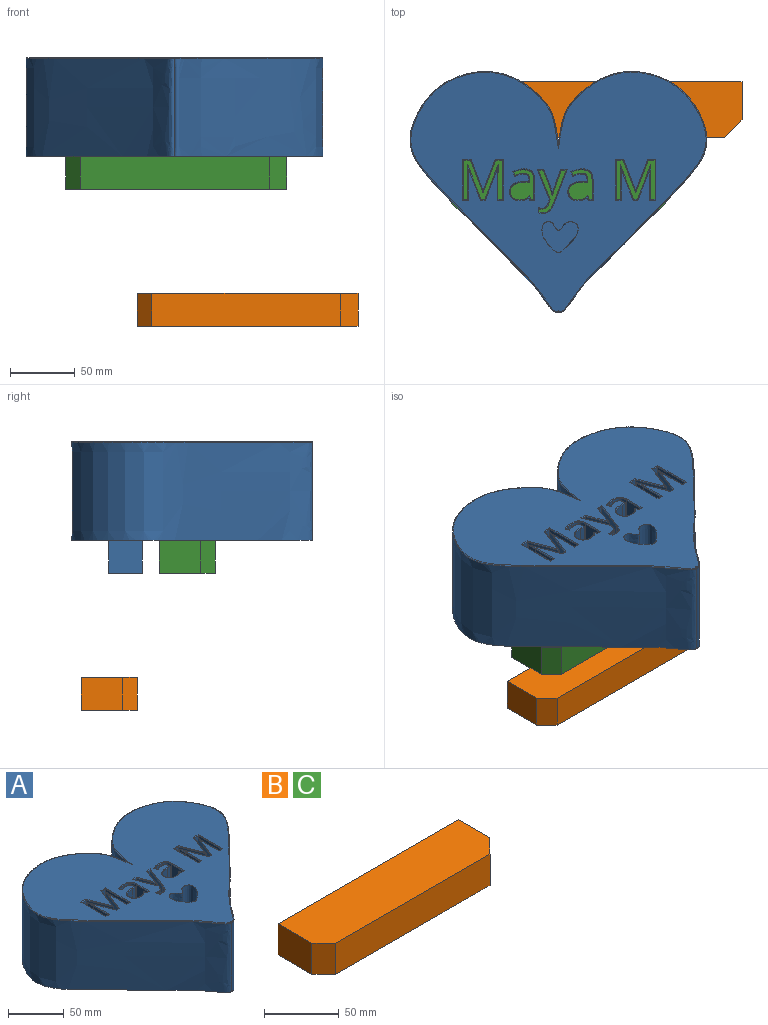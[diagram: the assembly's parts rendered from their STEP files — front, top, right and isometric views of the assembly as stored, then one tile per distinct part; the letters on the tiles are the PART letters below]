
ASSEMBLY  parts=3 mates=2
PART A: 183 faces, bbox 231.7x188.4x101.6 mm
  f0: plane 231.66x188.38mm, normal (0,0,-1), area 24079.3mm2, adj f2,f3,f4,f5,f6,f7,f8,f9
  f1: plane 227.62x184.41mm, normal (0,0,1), area 23045.1mm2, adj f94,f95,f96,f97,f98,f99,f100,f101
  f2: extruded ~184.82x114.31mm, area 26534mm2, adj f0,f3,f176
  f3: extruded ~184.82x114.31mm, area 26534mm2, adj f0,f2,f175
  f4: plane 75.57x3.68mm, normal (0,-1,0), area 278.4mm2, adj f0,f5,f19,f174
  f5: plane 75.57x22.78mm, normal (0.93,0.37,0), area 1854.8mm2, adj f0,f4,f6,f173
  f6: plane 75.57x3.22mm, normal (0.93,-0.37,0), area 261.5mm2, adj f0,f5,f7,f171
  f7: extruded ~75.57x5.05mm, area 520.7mm2, adj f0,f6,f8,f169
  f8: extruded ~75.57x2.54mm, area 193.2mm2, adj f0,f7,f9,f167
  f9: plane 75.57x2.75mm, normal (1,0,0), area 207.4mm2, adj f0,f8,f10,f165
  f10: extruded ~75.57x3.1mm, area 236.5mm2, adj f0,f9,f11,f163
  f11: extruded ~75.57x4.74mm, area 386.3mm2, adj f0,f10,f12,f161
  f12: extruded ~75.57x5.43mm, area 488.2mm2, adj f0,f11,f13,f160
  f13: plane 75.57x25.8mm, normal (-0.94,0.35,0), area 2083.6mm2, adj f0,f12,f14,f162
  f14: plane 75.57x3.68mm, normal (0,-1,0), area 277.9mm2, adj f0,f13,f15,f164
  f15: extruded ~75.57x15.7mm, area 1259.7mm2, adj f0,f14,f16,f166
  f16: extruded ~75.57x3.61mm, area 285.9mm2, adj f0,f15,f17,f168
  f17: plane 75.89x0.18mm, normal (0,-1,0), area 12.5mm2, adj f0,f16,f18,f168,f170
  f18: extruded ~75.57x6.39mm, area 506.9mm2, adj f0,f17,f19,f170
  f19: plane 75.57x12.92mm, normal (-0.93,-0.36,0), area 1045.7mm2, adj f0,f4,f18,f172
  f20: plane 75.57x26.79mm, normal (0.93,0.36,0), area 2167.5mm2, adj f0,f21,f37,f159
  f21: plane 75.57x2.83mm, normal (0,1,0), area 213.9mm2, adj f0,f20,f22,f158
  f22: plane 75.57x26.75mm, normal (-0.93,0.36,0), area 2167mm2, adj f0,f21,f23,f156
  f23: plane 75.89x0.18mm, normal (0,1,0), area 12.5mm2, adj f0,f22,f24,f154,f156
  f24: extruded ~75.57x7.28mm, area 550.4mm2, adj f0,f23,f25,f154
  f25: plane 75.57x19.47mm, normal (1,0,0), area 1471.5mm2, adj f0,f24,f26,f152
  f26: plane 75.57x3.51mm, normal (0,1,0), area 265.4mm2, adj f0,f25,f27,f150
  f27: plane 75.57x30.22mm, normal (-1,0,0), area 2283.7mm2, adj f0,f26,f28,f148
  f28: plane 75.57x5.25mm, normal (0,-1,0), area 396.9mm2, adj f0,f27,f29,f146
  f29: plane 75.57x24.93mm, normal (0.93,-0.36,0), area 2020.1mm2, adj f0,f28,f30,f145
  f30: plane 75.88x0.18mm, normal (0,-1,0), area 12.5mm2, adj f0,f29,f31,f145,f147
  f31: plane 75.57x24.93mm, normal (-0.93,-0.36,0), area 2017.9mm2, adj f0,f30,f32,f147
  f32: plane 75.57x5.29mm, normal (0,-1,0), area 399.9mm2, adj f0,f31,f33,f149
  f33: plane 75.57x30.22mm, normal (1,0,0), area 2283.7mm2, adj f0,f32,f34,f151
  f34: plane 75.57x3.25mm, normal (0,1,0), area 245.4mm2, adj f0,f33,f35,f153
  f35: plane 75.57x19.22mm, normal (-1,0,0), area 1452.5mm2, adj f0,f34,f36,f155
  f36: extruded ~75.57x7.57mm, area 572.4mm2, adj f0,f35,f37,f157
  f37: plane 75.89x0.18mm, normal (0,1,0), area 12.5mm2, adj f0,f20,f36,f157,f159
  f38: plane 75.57x3.23mm, normal (0.98,0.21,0), area 249.3mm2, adj f0,f39,f56,f144
  f39: plane 75.57x2.55mm, normal (0,1,0), area 192.4mm2, adj f0,f38,f40,f143
  f40: plane 75.57x15.47mm, normal (-1,0,0), area 1168.6mm2, adj f0,f39,f41,f141
  f41: extruded ~75.57x5.76mm, area 473.5mm2, adj f0,f40,f42,f139
  f42: extruded ~75.57x6mm, area 484.4mm2, adj f0,f41,f43,f137
  f43: extruded ~75.57x4.01mm, area 306mm2, adj f0,f42,f44,f135
  f44: extruded ~75.57x3.67mm, area 298mm2, adj f0,f43,f45,f133
  f45: plane 75.57x2.63mm, normal (0.93,0.37,0), area 213.9mm2, adj f0,f44,f46,f131
  f46: extruded ~75.57x6.4mm, area 505.4mm2, adj f0,f45,f47,f129
  f47: extruded ~75.57x3.67mm, area 302.4mm2, adj f0,f46,f48,f127
  f48: extruded ~75.57x3.94mm, area 316.6mm2, adj f0,f47,f49,f128
  f49: plane 75.57x1.41mm, normal (1,0,0), area 106.5mm2, adj f0,f48,f50,f130
  f50: plane 75.57x3.84mm, normal (0.03,-1,0), area 290.6mm2, adj f0,f49,f51,f132
  f51: extruded ~75.57x10.97mm, area 1113.9mm2, adj f0,f50,f52,f134
  f52: extruded ~75.57x4.94mm, area 412.8mm2, adj f0,f51,f53,f136
  f53: extruded ~75.57x5.28mm, area 429.9mm2, adj f0,f52,f54,f138
  f54: extruded ~75.57x4.21mm, area 325.6mm2, adj f0,f53,f55,f140
  f55: extruded ~75.57x3.38mm, area 338.8mm2, adj f0,f54,f56,f142
  f56: plane 75.89x0.2mm, normal (0,1,0), area 12.5mm2, adj f0,f38,f55,f142,f144
  f57: plane 75.57x3.23mm, normal (0.98,0.21,0), area 249.3mm2, adj f0,f58,f75,f126
  f58: plane 75.57x2.55mm, normal (0,1,0), area 192.4mm2, adj f0,f57,f59,f125
  f59: plane 75.57x15.47mm, normal (-1,0,0), area 1168.6mm2, adj f0,f58,f60,f123
  f60: extruded ~75.57x5.76mm, area 473.5mm2, adj f0,f59,f61,f121
  f61: extruded ~75.57x6mm, area 484.4mm2, adj f0,f60,f62,f119
  f62: extruded ~75.57x4.01mm, area 306mm2, adj f0,f61,f63,f117
  f63: extruded ~75.57x3.67mm, area 298mm2, adj f0,f62,f64,f115
  f64: plane 75.57x2.63mm, normal (0.93,0.37,0), area 213.9mm2, adj f0,f63,f65,f113
  f65: extruded ~75.57x6.4mm, area 505.4mm2, adj f0,f64,f66,f111
  f66: extruded ~75.57x3.67mm, area 302.4mm2, adj f0,f65,f67,f109
  f67: extruded ~75.57x3.94mm, area 316.6mm2, adj f0,f66,f68,f110
  f68: plane 75.57x1.41mm, normal (1,0,0), area 106.5mm2, adj f0,f67,f69,f112
  f69: plane 75.57x3.84mm, normal (0.03,-1,0), area 290.6mm2, adj f0,f68,f70,f114
  f70: extruded ~75.57x10.97mm, area 1113.9mm2, adj f0,f69,f71,f116
  f71: extruded ~75.57x4.94mm, area 412.8mm2, adj f0,f70,f72,f118
  f72: extruded ~75.57x5.28mm, area 429.9mm2, adj f0,f71,f73,f120
  f73: extruded ~75.57x4.21mm, area 325.6mm2, adj f0,f72,f74,f122
  f74: extruded ~75.57x3.38mm, area 338.8mm2, adj f0,f73,f75,f124
  f75: plane 75.89x0.2mm, normal (0,1,0), area 12.5mm2, adj f0,f57,f74,f124,f126
  f76: plane 75.57x26.79mm, normal (0.93,0.36,0), area 2167.5mm2, adj f0,f77,f93,f108
  f77: plane 75.57x2.83mm, normal (0,1,0), area 213.9mm2, adj f0,f76,f78,f107
  f78: plane 75.57x26.75mm, normal (-0.93,0.36,0), area 2167mm2, adj f0,f77,f79,f105
  f79: plane 75.89x0.18mm, normal (0,1,0), area 12.5mm2, adj f0,f78,f80,f103,f105
  f80: extruded ~75.57x7.28mm, area 550.4mm2, adj f0,f79,f81,f103
  f81: plane 75.57x19.47mm, normal (1,0,0), area 1471.5mm2, adj f0,f80,f82,f101
  f82: plane 75.57x3.51mm, normal (0,1,0), area 265.4mm2, adj f0,f81,f83,f99
  f83: plane 75.57x30.22mm, normal (-1,0,0), area 2283.7mm2, adj f0,f82,f84,f97
  f84: plane 75.57x5.25mm, normal (0,-1,0), area 396.9mm2, adj f0,f83,f85,f95
  f85: plane 75.57x24.93mm, normal (0.93,-0.36,0), area 2020.1mm2, adj f0,f84,f86,f94
  f86: plane 75.88x0.18mm, normal (0,-1,0), area 12.5mm2, adj f0,f85,f87,f94,f96
  f87: plane 75.57x24.93mm, normal (-0.93,-0.36,0), area 2017.9mm2, adj f0,f86,f88,f96
  f88: plane 75.57x5.29mm, normal (0,-1,0), area 399.9mm2, adj f0,f87,f89,f98
  f89: plane 75.57x30.22mm, normal (1,0,0), area 2283.7mm2, adj f0,f88,f90,f100
  f90: plane 75.57x3.25mm, normal (0,1,0), area 245.4mm2, adj f0,f89,f91,f102
  f91: plane 75.57x19.22mm, normal (-1,0,0), area 1452.5mm2, adj f0,f90,f92,f104
  f92: extruded ~75.57x7.57mm, area 572.4mm2, adj f0,f91,f93,f106
  f93: plane 75.89x0.18mm, normal (0,1,0), area 12.5mm2, adj f0,f76,f92,f106,f108
  f94: cylinder r=0.64mm len=25.59mm, axis (0.36,0.93,0), area 26.4mm2, adj f1,f85,f86,f95,f96
  f95: cylinder r=0.64mm len=6.32mm, axis (1,0,0), area 5.8mm2, adj f1,f84,f94,f97
  f96: cylinder r=0.64mm len=25.59mm, axis (0.36,-0.93,0), area 26.4mm2, adj f1,f86,f87,f94,f98
  f97: cylinder r=0.64mm len=31.49mm, axis (0,-1,0), area 30.8mm2, adj f1,f83,f95,f99
  f98: cylinder r=0.64mm len=6.36mm, axis (1,0,0), area 5.8mm2, adj f1,f88,f96,f100
  f99: cylinder r=0.64mm len=4.78mm, axis (-1,0,0), area 4.1mm2, adj f1,f82,f97,f101
  f100: cylinder r=0.64mm len=31.49mm, axis (0,1,0), area 30.8mm2, adj f1,f89,f98,f102
  f101: cylinder r=0.64mm len=20.11mm, axis (0,1,0), area 19.7mm2, adj f1,f81,f99,f103
  f102: cylinder r=0.64mm len=4.52mm, axis (-1,0,0), area 3.9mm2, adj f1,f90,f100,f104
  f103: bspline ~10.89x1.07mm, area 6.1mm2, adj f1,f79,f80,f101,f105
  f104: cylinder r=0.64mm len=19.86mm, axis (0,-1,0), area 19.5mm2, adj f1,f91,f102,f106
  f105: cylinder r=0.64mm len=27.41mm, axis (-0.36,-0.93,0), area 27.6mm2, adj f1,f78,f79,f103,f107
  f106: bspline ~9.93x0.97mm, area 6.4mm2, adj f1,f92,f93,f104,f108
  f107: cylinder r=0.64mm len=3.7mm, axis (-1,0,0), area 3.3mm2, adj f1,f77,f105,f108
  f108: cylinder r=0.64mm len=27.45mm, axis (-0.36,0.93,0), area 27.6mm2, adj f1,f76,f93,f106,f107
  f109: bspline ~5.42x2.18mm, area 3.8mm2, adj f1,f66,f110,f111
  f110: bspline ~6.23x2.17mm, area 4mm2, adj f1,f67,f109,f112
  f111: bspline ~9.07x2.76mm, area 6.9mm2, adj f1,f65,f109,f113
  f112: cylinder r=0.64mm len=1.41mm, axis (0,1,0), area 1.1mm2, adj f1,f68,f110,f114
  f113: cylinder r=0.64mm len=4.02mm, axis (-0.37,0.93,0), area 3.4mm2, adj f1,f64,f111,f115
  f114: cylinder r=0.64mm len=3.86mm, axis (1,0.03,0), area 3.5mm2, adj f1,f69,f112,f116
  f115: bspline ~7.51x3.71mm, area 4.3mm2, adj f1,f63,f113,f117
  f116: bspline ~16.18x10.25mm, area 15.1mm2, adj f1,f70,f114,f118
  f117: bspline ~5.57x1.33mm, area 4.1mm2, adj f1,f62,f115,f119
  f118: bspline ~7.83x3.22mm, area 5.6mm2, adj f1,f71,f116,f120
  f119: bspline ~10x3.31mm, area 6.6mm2, adj f1,f61,f117,f121
  f120: bspline ~7.09x3.13mm, area 5.8mm2, adj f1,f72,f118,f122
  f121: bspline ~9.19x3.4mm, area 6.4mm2, adj f1,f60,f119,f123
  f122: bspline ~6.18x1.76mm, area 4.4mm2, adj f1,f73,f120,f124
  f123: cylinder r=0.64mm len=16.1mm, axis (0,-1,0), area 15.7mm2, adj f1,f59,f121,f125
  f124: bspline ~5.25x4.3mm, area 4.2mm2, adj f1,f74,f75,f122,f126
  f125: cylinder r=0.64mm len=3.7mm, axis (-1,0,0), area 3.1mm2, adj f1,f58,f123,f126
  f126: cylinder r=0.64mm len=3.88mm, axis (-0.21,0.98,0), area 3.2mm2, adj f1,f57,f75,f124,f125
  f127: bspline ~5.42x2.18mm, area 3.8mm2, adj f1,f47,f128,f129
  f128: bspline ~6.23x2.17mm, area 4mm2, adj f1,f48,f127,f130
  f129: bspline ~9.07x2.76mm, area 6.9mm2, adj f1,f46,f127,f131
  f130: cylinder r=0.64mm len=1.41mm, axis (0,1,0), area 1.1mm2, adj f1,f49,f128,f132
  f131: cylinder r=0.64mm len=4.02mm, axis (-0.37,0.93,0), area 3.4mm2, adj f1,f45,f129,f133
  f132: cylinder r=0.64mm len=3.86mm, axis (1,0.03,0), area 3.5mm2, adj f1,f50,f130,f134
  f133: bspline ~7.51x3.71mm, area 4.3mm2, adj f1,f44,f131,f135
  f134: bspline ~16.18x10.25mm, area 15.1mm2, adj f1,f51,f132,f136
  f135: bspline ~5.57x1.33mm, area 4.1mm2, adj f1,f43,f133,f137
  f136: bspline ~7.83x3.22mm, area 5.6mm2, adj f1,f52,f134,f138
  f137: bspline ~10x3.31mm, area 6.6mm2, adj f1,f42,f135,f139
  f138: bspline ~8.76x3.13mm, area 5.8mm2, adj f1,f53,f136,f140
  f139: bspline ~9.19x3.4mm, area 6.4mm2, adj f1,f41,f137,f141
  f140: bspline ~6.18x1.76mm, area 4.4mm2, adj f1,f54,f138,f142
  f141: cylinder r=0.64mm len=16.1mm, axis (0,-1,0), area 15.7mm2, adj f1,f40,f139,f143
  f142: bspline ~5.25x4.3mm, area 4.2mm2, adj f1,f55,f56,f140,f144
  f143: cylinder r=0.64mm len=3.7mm, axis (-1,0,0), area 3.1mm2, adj f1,f39,f141,f144
  f144: cylinder r=0.64mm len=3.88mm, axis (-0.21,0.98,0), area 3.2mm2, adj f1,f38,f56,f142,f143
  f145: cylinder r=0.64mm len=25.59mm, axis (0.36,0.93,0), area 26.4mm2, adj f1,f29,f30,f146,f147
  f146: cylinder r=0.64mm len=6.32mm, axis (1,0,0), area 5.8mm2, adj f1,f28,f145,f148
  f147: cylinder r=0.64mm len=25.59mm, axis (0.36,-0.93,0), area 26.4mm2, adj f1,f30,f31,f145,f149
  f148: cylinder r=0.64mm len=31.49mm, axis (0,-1,0), area 30.8mm2, adj f1,f27,f146,f150
  f149: cylinder r=0.64mm len=6.36mm, axis (1,0,0), area 5.8mm2, adj f1,f32,f147,f151
  f150: cylinder r=0.64mm len=4.78mm, axis (-1,0,0), area 4.1mm2, adj f1,f26,f148,f152
  f151: cylinder r=0.64mm len=31.49mm, axis (0,1,0), area 30.8mm2, adj f1,f33,f149,f153
  f152: cylinder r=0.64mm len=20.11mm, axis (0,1,0), area 19.7mm2, adj f1,f25,f150,f154
  f153: cylinder r=0.64mm len=4.52mm, axis (-1,0,0), area 3.9mm2, adj f1,f34,f151,f155
  f154: bspline ~10.89x1.07mm, area 6.1mm2, adj f1,f23,f24,f152,f156
  f155: cylinder r=0.64mm len=19.86mm, axis (0,-1,0), area 19.5mm2, adj f1,f35,f153,f157
  f156: cylinder r=0.64mm len=27.41mm, axis (-0.36,-0.93,0), area 27.6mm2, adj f1,f22,f23,f154,f158
  f157: bspline ~9.93x0.97mm, area 6.4mm2, adj f1,f36,f37,f155,f159
  f158: cylinder r=0.64mm len=3.7mm, axis (-1,0,0), area 3.3mm2, adj f1,f21,f156,f159
  f159: cylinder r=0.64mm len=27.45mm, axis (-0.36,0.93,0), area 27.6mm2, adj f1,f20,f37,f157,f158
  f160: bspline ~7.16x5.2mm, area 6.6mm2, adj f1,f12,f161,f162
  f161: bspline ~6.96x2.89mm, area 5.3mm2, adj f1,f11,f160,f163
  f162: cylinder r=0.64mm len=26.88mm, axis (-0.35,-0.94,0), area 28mm2, adj f1,f13,f160,f164
  f163: bspline ~6.1x1.5mm, area 3.4mm2, adj f1,f10,f161,f165
  f164: cylinder r=0.64mm len=5.04mm, axis (1,0,0), area 4.3mm2, adj f1,f14,f162,f166
  f165: cylinder r=0.64mm len=4.04mm, axis (0,1,0), area 3.4mm2, adj f1,f9,f163,f167
  f166: bspline ~22.75x8.65mm, area 16.9mm2, adj f1,f15,f164,f168
  f167: bspline ~5.6x1.39mm, area 2.9mm2, adj f1,f8,f165,f169
  f168: bspline ~5.36x2.2mm, area 3.1mm2, adj f1,f16,f17,f166,f170
  f169: bspline ~6.86x4.48mm, area 6.6mm2, adj f1,f7,f167,f171
  f170: bspline ~8.01x3.1mm, area 6.1mm2, adj f1,f17,f18,f168,f172
  f171: cylinder r=0.64mm len=3.46mm, axis (0.37,0.93,0), area 3.3mm2, adj f1,f6,f169,f173
  f172: cylinder r=0.64mm len=13.56mm, axis (0.36,-0.93,0), area 14mm2, adj f1,f19,f170,f174
  f173: cylinder r=0.64mm len=23.89mm, axis (-0.37,0.93,0), area 24.8mm2, adj f1,f5,f171,f174
  f174: cylinder r=0.64mm len=5.06mm, axis (1,0,0), area 4.4mm2, adj f1,f4,f172,f173
  f175: bspline ~185.69x115.29mm, area 351.6mm2, adj f1,f3,f176
  f176: bspline ~185.69x115.29mm, area 351.6mm2, adj f1,f2,f175
  f177: extruded ~50.8x27.95mm, area 4522.2mm2, adj f1,f178
  f178: plane 28.79x24.74mm, normal (0,0,1), area 452.6mm2, adj f177
  f179: plane 25.49x25.4mm, normal (0.86,-0.5,0), area 750mm2, adj f0,f180,f181,f182
  f180: plane 29.53x25.4mm, normal (0.01,1,0), area 750mm2, adj f0,f179,f181,f182
  f181: plane 25.65x25.4mm, normal (-0.87,-0.5,0), area 750mm2, adj f0,f179,f180,f182
  f182: plane 29.53x25.65mm, normal (0,0,-1), area 377.5mm2, adj f179,f180,f181
PART B: 8 faces, bbox 170.2x43.2x25.4 mm
  f0: plane 25.4x11.26mm, normal (-0.71,-0.7,0), area 402.7mm2, adj f1,f5,f6,f7
  f1: plane 145.54x25.4mm, normal (0,-1,0), area 3696.8mm2, adj f0,f2,f6,f7
  f2: plane 25.4x13.67mm, normal (0.71,-0.7,0), area 487.6mm2, adj f1,f3,f6,f7
  f3: plane 29.51x25.4mm, normal (1,0,0), area 749.5mm2, adj f2,f4,f6,f7
  f4: plane 170.18x25.4mm, normal (0,1,0), area 4322.6mm2, adj f3,f5,f6,f7
  f5: plane 31.92x25.4mm, normal (-1,0,0), area 810.7mm2, adj f0,f4,f6,f7
  f6: plane 170.18x43.18mm, normal (0,0,-1), area 7193.4mm2, adj f0,f1,f2,f3,f4,f5
  f7: plane 170.18x43.18mm, normal (0,0,1), area 7193.4mm2, adj f0,f1,f2,f3,f4,f5
PART C: same geometry as B
PLACE A t=(-254.2,-292.4,-1.42)mm
PLACE B t=(-198.95,-233.03,-107.08)mm
PLACE C t=(-254.03,-293.2,-1.42)mm
MATE slider A.f182 <-> B.f7  axis (0,0,-1) through (-198.16,-252.96,-26.82)mm
MATE fastened C.f7 <-> A.f0  axis (0,0,1) through (-253.25,-313.13,-1.42)mm
